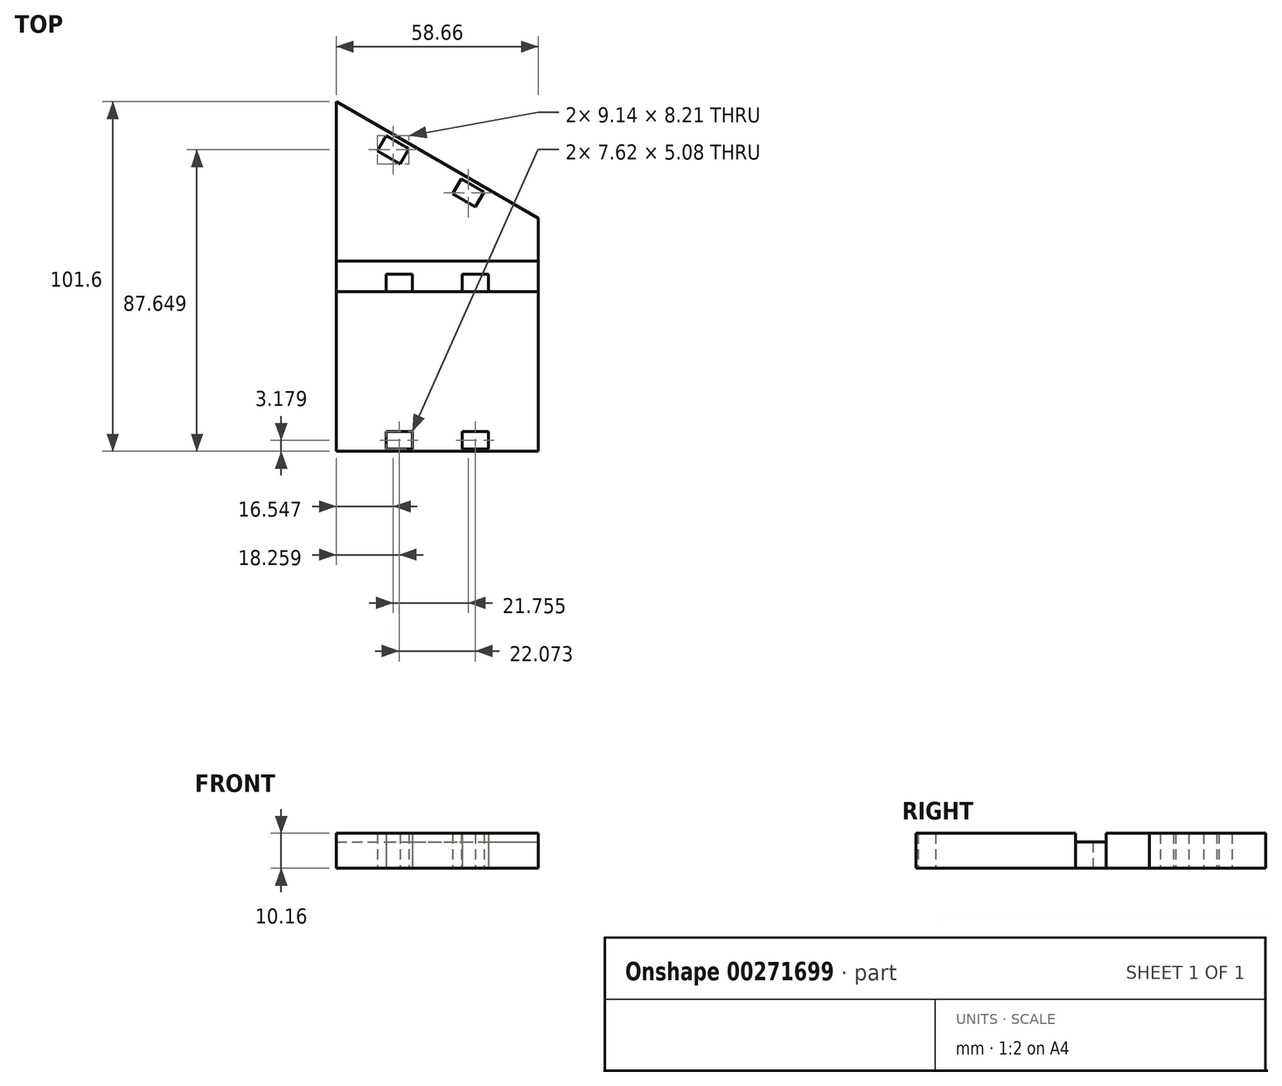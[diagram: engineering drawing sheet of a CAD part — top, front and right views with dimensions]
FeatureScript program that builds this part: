
annotation { "Feature Type Name" : "Feature", "Feature Type Description" : "" }
export const myFeature = defineFeature(function(context is Context, id is Id, definition is map)
    precondition{}
    {
        {
            var Q0;
            Q0=qCreatedBy(makeId("Top.planeOp"),FACE);
            var sketch = newSketch(context, id + "F0", { "sketchPlane" : qUnion([Q0])});
            skLineSegment(sketch, "E0", {"start": v(-23.12, -21.87) * mm, "end": v(-23.12, -123.47) * mm});
            skLineSegment(sketch, "E1", {"start": v(-23.12, -123.47) * mm, "end": v(35.54, -123.47) * mm});
            skLineSegment(sketch, "E2", {"start": v(35.54, -123.47) * mm, "end": v(35.54, -55.73) * mm});
            skLineSegment(sketch, "E3", {"start": v(35.54, -55.73) * mm, "end": v(-23.12, -21.87) * mm});
            skLineSegment(sketch, "E4", {"start": v(-23.12, -117.75) * mm, "end": v(35.54, -117.75) * mm, "construction": true});
            skLineSegment(sketch, "E5.bottom", {"start": v(-8.67, -117.75) * mm, "end": v(-1.05, -117.75) * mm});
            skLineSegment(sketch, "E5.top", {"start": v(-8.67, -122.83) * mm, "end": v(-1.05, -122.83) * mm});
            skLineSegment(sketch, "E5.left", {"start": v(-8.67, -117.75) * mm, "end": v(-8.67, -122.83) * mm});
            skLineSegment(sketch, "E5.right", {"start": v(-1.05, -117.75) * mm, "end": v(-1.05, -122.83) * mm});
            skLineSegment(sketch, "E6.top", {"start": v(8.8, -123.47) * mm, "end": v(25.31, -123.47) * mm});
            skLineSegment(sketch, "E7.bottom", {"start": v(13.4, -117.76) * mm, "end": v(21.02, -117.76) * mm});
            skLineSegment(sketch, "E7.top", {"start": v(13.4, -122.84) * mm, "end": v(21.02, -122.84) * mm});
            skLineSegment(sketch, "E7.left", {"start": v(13.4, -117.76) * mm, "end": v(13.4, -122.84) * mm});
            skLineSegment(sketch, "E7.right", {"start": v(21.02, -117.76) * mm, "end": v(21.02, -122.84) * mm});
            skLineSegment(sketch, "E8", {"start": v(-23.12, -29.2) * mm, "end": v(35.54, -63.07) * mm, "construction": true});
            skLineSegment(sketch, "E9", {"start": v(-8.6, -31.72) * mm, "end": v(-11.14, -36.12) * mm});
            skLineSegment(sketch, "E10", {"start": v(-11.14, -36.12) * mm, "end": v(-4.54, -39.93) * mm});
            skLineSegment(sketch, "E11", {"start": v(-41.2, -53.17) * mm, "end": v(-7.16, 5.78) * mm, "construction": true});
            skLineSegment(sketch, "E12", {"start": v(18.57, -85.12) * mm, "end": v(55.65, -20.89) * mm, "construction": true});
            skLineSegment(sketch, "E13.top", {"start": v(10.61, -48.68) * mm, "end": v(17.21, -52.49) * mm});
            skLineSegment(sketch, "E13.left", {"start": v(13.15, -44.28) * mm, "end": v(10.61, -48.68) * mm});
            skLineSegment(sketch, "E14", {"start": v(-4.54, -39.93) * mm, "end": v(-2, -35.53) * mm});
            skLineSegment(sketch, "E15", {"start": v(-8.6, -31.72) * mm, "end": v(-2, -35.53) * mm});
            skLineSegment(sketch, "E16", {"start": v(17.21, -52.49) * mm, "end": v(19.75, -48.09) * mm});
            skLineSegment(sketch, "E17", {"start": v(13.15, -44.28) * mm, "end": v(19.75, -48.09) * mm});
            skLineSegment(sketch, "E18", {"start": v(-23.12, -68.22) * mm, "end": v(35.54, -68.22) * mm});
            skLineSegment(sketch, "E19", {"start": v(-23.12, -77.11) * mm, "end": v(35.54, -77.11) * mm});
            skLineSegment(sketch, "E20.bottom", {"start": v(-8.67, -72.03) * mm, "end": v(-1.05, -72.03) * mm});
            skLineSegment(sketch, "E20.top", {"start": v(-8.67, -77.11) * mm, "end": v(-1.05, -77.11) * mm});
            skLineSegment(sketch, "E20.left", {"start": v(-8.67, -72.03) * mm, "end": v(-8.67, -77.11) * mm});
            skLineSegment(sketch, "E20.right", {"start": v(-1.05, -72.03) * mm, "end": v(-1.05, -77.11) * mm});
            skLineSegment(sketch, "E21.bottom", {"start": v(13.4, -72.03) * mm, "end": v(21.02, -72.03) * mm});
            skLineSegment(sketch, "E21.top", {"start": v(13.4, -77.11) * mm, "end": v(21.02, -77.11) * mm});
            skLineSegment(sketch, "E21.left", {"start": v(13.4, -72.03) * mm, "end": v(13.4, -77.11) * mm});
            skLineSegment(sketch, "E21.right", {"start": v(21.02, -72.03) * mm, "end": v(21.02, -77.11) * mm});
            skSolve(sketch);
        }
        {
            var Q0;
            {var subQ0=sQuery(id+"F0.wireOp",EDGE,"E3");Q0=makeQuery(id+"F0.imprint","IMPRINT",FACE,{"disambiguationData":[TD([[makeQuery(id+"F0.imprint","IMPRINT",EDGE,{"derivedFrom":subQ0}),1.0]])]});}
            var Q1;
            Q1=makeQuery(id+"F0.imprint","IMPRINT",FACE,{"disambiguationData":[TD([[makeQuery(id+"F0.imprint","IMPRINT",EDGE,{"derivedFrom":sQuery(id+"F0.wireOp",EDGE,"E5.bottom")}),1.0]])]});
            extrude(context, id + "F1", {"entities" : qUnion([Q0, Q1]), "depth" : 10.16 * mm});
        }
        {
            var Q0;
            {var subQ0=sQuery(id+"F0.wireOp",EDGE,"E18");Q0=makeQuery(id+"F0.imprint","IMPRINT",FACE,{"disambiguationData":[TD([[makeQuery(id+"F0.imprint","IMPRINT",EDGE,{"derivedFrom":subQ0}),-1.0]])]});}
            extrude(context, id + "F2", {"entities" : qUnion([Q0]), "depth" : 7.62 * mm});
        }
    });
